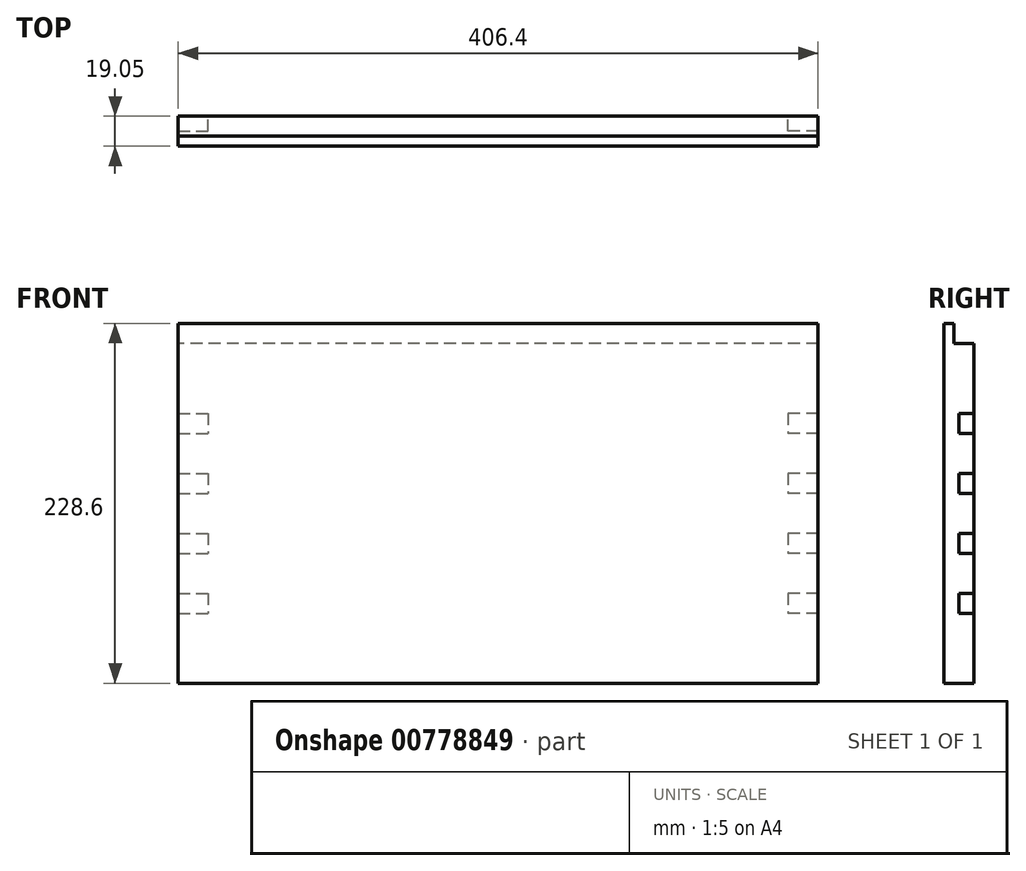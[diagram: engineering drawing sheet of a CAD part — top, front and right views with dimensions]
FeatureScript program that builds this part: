
annotation { "Feature Type Name" : "Feature", "Feature Type Description" : "" }
export const myFeature = defineFeature(function(context is Context, id is Id, definition is map)
    precondition{}
    {
        {
            var Q0;
            Q0=qCreatedBy(makeId("Front.planeOp"),FACE);
            var sketch = newSketch(context, id + "F0", { "sketchPlane" : qUnion([Q0])});
            skLineSegment(sketch, "E0.bottom", {"start": v(-203.2, -114.3) * mm, "end": v(203.2, -114.3) * mm});
            skLineSegment(sketch, "E0.top", {"start": v(-203.2, 114.3) * mm, "end": v(203.2, 114.3) * mm});
            skLineSegment(sketch, "E0.left", {"start": v(-203.2, -114.3) * mm, "end": v(-203.2, 114.3) * mm});
            skLineSegment(sketch, "E0.right", {"start": v(203.2, -114.3) * mm, "end": v(203.2, 114.3) * mm});
            skPoint(sketch, "E0.middle", {"position": v(0, 0) * mm});
            skSolve(sketch);
        }
        {
            var Q0;
            Q0=makeQuery(id+"F0.imprint","IMPRINT",FACE,{"disambiguationData":[TD([[makeQuery(id+"F0.imprint","IMPRINT",EDGE,{"derivedFrom":sQuery(id+"F0.wireOp",EDGE,"E0.bottom")}),1.0]])]});
            var Q1;
            Q1=sQuery(id+"F0.wireOp",EDGE,"E0.top");
            var Q2;
            Q2=sQuery(id+"F0.wireOp",EDGE,"E0.right");
            var Q3;
            Q3=sQuery(id+"F0.wireOp",EDGE,"E0.left");
            var Q4;
            Q4=sQuery(id+"F0.wireOp",EDGE,"E0.bottom");
            extrude(context, id + "F1", {"entities" : qUnion([Q0]), "surfaceEntities" : qUnion([Q1, Q2, Q3, Q4]), "depth" : 19.05 * mm, "offsetDistance" : 25.4 * mm});
        }
        {
            var Q0;
            Q0=makeQuery(id+"F1.opExtrude","SWEPT_FACE",FACE,{"disambiguationData":[OSD([sQuery(id+"F0.wireOp",EDGE,"E0.left")])]});
            var sketch = newSketch(context, id + "F2", { "sketchPlane" : qUnion([Q0])});
            skPoint(sketch, "E1.oppositeSnap0", {"position": v(12.7, 117.01) * mm});
            skLineSegment(sketch, "E1.bottom", {"start": v(0, 114.3) * mm, "end": v(12.7, 114.3) * mm});
            skLineSegment(sketch, "E1.top", {"start": v(0, 101.6) * mm, "end": v(12.7, 101.6) * mm});
            skLineSegment(sketch, "E1.left", {"start": v(0, 114.3) * mm, "end": v(0, 101.6) * mm});
            skLineSegment(sketch, "E1.right", {"start": v(12.7, 114.3) * mm, "end": v(12.7, 101.6) * mm});
            skSolve(sketch);
        }
        {
            var Q0;
            Q0=makeQuery(id+"F2.imprint","IMPRINT",FACE,{"disambiguationData":[TD([[makeQuery(id+"F2.imprint","IMPRINT",EDGE,{"derivedFrom":sQuery(id+"F2.wireOp",EDGE,"E1.bottom")}),1.0]])]});
            extrude(context, id + "F3", {"entities" : qUnion([Q0]), "operationType" : NewBodyOperationType.REMOVE, "endBound" : BoundingType.UP_TO_NEXT, "oppositeDirection" : true, "depth" : 25.4 * mm, "offsetDistance" : 25.4 * mm});
        }
        {
            var Q0;
            Q0=makeQuery(id+"F1.opExtrude","CAP_FACE",FACE,{"disambiguationData":[OSD([sQuery(id+"F0.wireOp",EDGE,"E0.bottom"),sQuery(id+"F0.wireOp",EDGE,"E0.top"),sQuery(id+"F0.wireOp",EDGE,"E0.left"),sQuery(id+"F0.wireOp",EDGE,"E0.right")])],"isStart":true});
            var sketch = newSketch(context, id + "F4", { "sketchPlane" : qUnion([Q0])});
            skLineSegment(sketch, "E2", {"start": v(0, 101.6) * mm, "end": v(0, -114.3) * mm, "construction": true});
            skLineSegment(sketch, "E3", {"start": v(-203.2, 0) * mm, "end": v(203.2, 0) * mm});
            skLineSegment(sketch, "E4.bottom", {"start": v(-203.2, 57.15) * mm, "end": v(-184.15, 57.15) * mm});
            skLineSegment(sketch, "E4.top", {"start": v(-203.2, 44.45) * mm, "end": v(-184.15, 44.45) * mm});
            skLineSegment(sketch, "E4.left", {"start": v(-203.2, 57.15) * mm, "end": v(-203.2, 44.45) * mm});
            skLineSegment(sketch, "E4.right", {"start": v(-184.15, 57.15) * mm, "end": v(-184.15, 44.45) * mm});
            skLineSegment(sketch, "E5.bottom", {"start": v(-203.2, 19.05) * mm, "end": v(-184.15, 19.05) * mm});
            skLineSegment(sketch, "E5.top", {"start": v(-203.2, 6.35) * mm, "end": v(-184.15, 6.35) * mm});
            skLineSegment(sketch, "E5.left", {"start": v(-203.2, 19.05) * mm, "end": v(-203.2, 6.35) * mm});
            skLineSegment(sketch, "E5.right", {"start": v(-184.15, 19.05) * mm, "end": v(-184.15, 6.35) * mm});
            skLineSegment(sketch, "E6.bottom", {"start": v(-203.2, -19.05) * mm, "end": v(-184.15, -19.05) * mm});
            skLineSegment(sketch, "E6.top", {"start": v(-203.2, -31.75) * mm, "end": v(-184.15, -31.75) * mm});
            skLineSegment(sketch, "E6.left", {"start": v(-203.2, -19.05) * mm, "end": v(-203.2, -31.75) * mm});
            skLineSegment(sketch, "E6.right", {"start": v(-184.15, -19.05) * mm, "end": v(-184.15, -31.75) * mm});
            skLineSegment(sketch, "E7.bottom", {"start": v(-203.2, -57.15) * mm, "end": v(-184.15, -57.15) * mm});
            skLineSegment(sketch, "E7.top", {"start": v(-203.2, -69.85) * mm, "end": v(-184.15, -69.85) * mm});
            skLineSegment(sketch, "E7.left", {"start": v(-203.2, -57.15) * mm, "end": v(-203.2, -69.85) * mm});
            skLineSegment(sketch, "E7.right", {"start": v(-184.15, -57.15) * mm, "end": v(-184.15, -69.85) * mm});
            skLineSegment(sketch, "E8.MirrorCS", {"start": v(184.15, 57.15) * mm, "end": v(184.15, 44.45) * mm});
            skLineSegment(sketch, "E9.MirrorCS", {"start": v(203.2, 57.15) * mm, "end": v(184.15, 57.15) * mm});
            skLineSegment(sketch, "E10.MirrorCS", {"start": v(203.2, 57.15) * mm, "end": v(203.2, 44.45) * mm});
            skLineSegment(sketch, "E11.MirrorCS", {"start": v(203.2, 44.45) * mm, "end": v(184.15, 44.45) * mm});
            skLineSegment(sketch, "E12.MirrorCS", {"start": v(203.2, 19.05) * mm, "end": v(184.15, 19.05) * mm});
            skLineSegment(sketch, "E13.MirrorCS", {"start": v(184.15, 19.05) * mm, "end": v(184.15, 6.35) * mm});
            skLineSegment(sketch, "E14.MirrorCS", {"start": v(203.2, 6.35) * mm, "end": v(184.15, 6.35) * mm});
            skLineSegment(sketch, "E15.MirrorCS", {"start": v(203.2, 19.05) * mm, "end": v(203.2, 6.35) * mm});
            skLineSegment(sketch, "E16.MirrorCS", {"start": v(203.2, -19.05) * mm, "end": v(184.15, -19.05) * mm});
            skLineSegment(sketch, "E17.MirrorCS", {"start": v(203.2, -19.05) * mm, "end": v(203.2, -31.75) * mm});
            skLineSegment(sketch, "E18.MirrorCS", {"start": v(203.2, -31.75) * mm, "end": v(184.15, -31.75) * mm});
            skLineSegment(sketch, "E19.MirrorCS", {"start": v(184.15, -19.05) * mm, "end": v(184.15, -31.75) * mm});
            skLineSegment(sketch, "E20.MirrorCS", {"start": v(203.2, -57.15) * mm, "end": v(203.2, -69.85) * mm});
            skLineSegment(sketch, "E21.MirrorCS", {"start": v(203.2, -57.15) * mm, "end": v(184.15, -57.15) * mm});
            skLineSegment(sketch, "E22.MirrorCS", {"start": v(184.15, -57.15) * mm, "end": v(184.15, -69.85) * mm});
            skLineSegment(sketch, "E23.MirrorCS", {"start": v(203.2, -69.85) * mm, "end": v(184.15, -69.85) * mm});
            skSolve(sketch);
        }
        {
            var Q0;
            Q0 = qSketchRegion(id + "F4", true);
            extrude(context, id + "F5", {"entities" : qUnion([Q0]), "operationType" : NewBodyOperationType.REMOVE, "oppositeDirection" : true, "depth" : 9.52 * mm, "offsetDistance" : 25.4 * mm});
        }
    });
